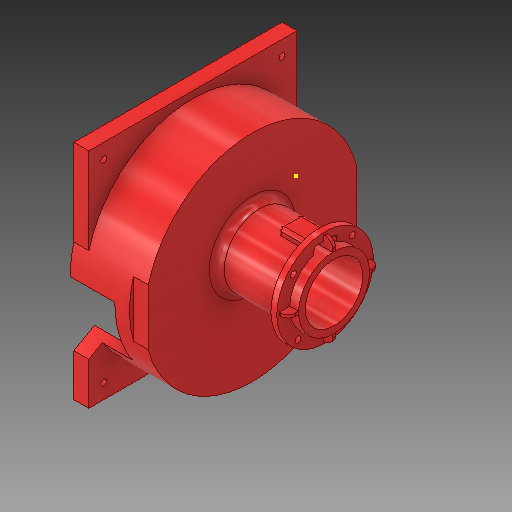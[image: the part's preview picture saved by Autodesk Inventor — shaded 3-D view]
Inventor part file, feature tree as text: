
AUTODESK INVENTOR PART (.ipt)
format: ipt  version: 2019 (Build 230136000, 136)  size: 1,012,736 bytes
history: native  units: mm
features: sketch x42, extrude x40, projected_geometry x19, other x6, fillet x6, reference x2
ambient origin geometry x8: Origin, YZ Plane, XZ Plane, XY Plane, X Axis, Y Axis, Z Axis, Center Point
bodies: Body1 (feature_tree)
feature tree (115):
  other  "Твердое тело1"
  other  "0ae4c1a17e304db4a8c8e39318f74883.stl"
  extrude  "Выдавливание1"  Depth=3.0mm TaperAngle=0.0deg
  extrude  "Выдавливание2"  Depth=43.0mm
  extrude  "Выдавливание3"  Depth=25.0mm TaperAngle=0.0deg
  extrude  "Выдавливание4"  Depth=20.0mm
  extrude  "Выдавливание5"  Depth=20.0mm
  extrude  "Выдавливание6"  Depth=50.0mm TaperAngle=0.0deg
  extrude  "Выдавливание7"  Depth=34.0mm
  extrude  "Выдавливание8"  Depth=2.0mm
  extrude  "Выдавливание9"  Depth=2.0mm
  extrude  "Выдавливание10"  Depth=1.0mm TaperAngle=0.0deg
  sketch  "Эскиз15"
  sketch  "Эскиз16"
  extrude  "Выдавливание11"  Depth=25.0mm TaperAngle=0.0deg
  extrude  "Выдавливание12"  Depth=4.0mm
  extrude  "Выдавливание13"  Depth=4.0mm
  extrude  "Выдавливание14"  Depth=4.0mm
  extrude  "Выдавливание15"  Depth=4.0mm
  extrude  "Выдавливание16"  Depth=4.5mm
  fillet  "Сопряжение1"  Radius=4.5mm
  fillet  "Сопряжение2"  Radius=4.5mm
  extrude  "Выдавливание17"  Depth=4.5mm
  extrude  "Выдавливание18"  Depth=25.0mm TaperAngle=0.0deg
  extrude  "Выдавливание19"  Depth=7.2mm
  extrude  "Выдавливание20"  Depth=7.2mm
  extrude  "Выдавливание21"  Depth=7.2mm
  extrude  "Выдавливание22"  Depth=7.2mm
  fillet  "Сопряжение3"  Radius=2.0mm
  extrude  "Выдавливание23"  Depth=15.0mm TaperAngle=0.0deg
  extrude  "Выдавливание24"  Depth=15.0mm
  extrude  "Выдавливание25"  Depth=3.0mm
  extrude  "Выдавливание26"  Depth=13.663525mm
  extrude  "Выдавливание27"  Depth=30.32705mm
  extrude  "Выдавливание28"  Depth=8.5mm TaperAngle=0.0deg
  fillet  "Сопряжение4"  Radius=8.5mm
  extrude  "Выдавливание29"  Depth=38.8mm
  extrude  "Выдавливание30"  Depth=22.0mm TaperAngle=0.0deg
  extrude  "Выдавливание31"  Depth=25.0mm TaperAngle=0.0deg
  extrude  "Выдавливание32"  Depth=10.0mm TaperAngle=0.0deg
  fillet  "Сопряжение5"  Radius=3.5mm
  sketch  "Эскиз38"
  extrude  "Выдавливание33"  Depth=3.5mm TaperAngle=0.0deg
  extrude  "Выдавливание34"  Depth=1.0mm TaperAngle=0.0deg
  extrude  "Выдавливание35"  Depth=2.0mm
  fillet  "Сопряжение6"  Radius=2.0mm
  extrude  "Выдавливание37"  Depth=10.0mm TaperAngle=0.0deg
  extrude  "Выдавливание38"  Depth=3.0mm TaperAngle=0.0deg
  extrude  "Выдавливание39"  Depth=3.0mm TaperAngle=0.0deg
  extrude  "Выдавливание40"  Depth=28.0mm
  extrude  "Выдавливание41"  TaperAngle=135.0deg  [1 undecoded]
  sketch  "Эскиз2"
  sketch  "Эскиз3"
  sketch  "Эскиз5"
  sketch  "Эскиз6"
  projected_geometry  "Спроецированная петля1"
  sketch  "Эскиз8"
  sketch  "Эскиз9"
  projected_geometry  "Спроецированная петля3"
  sketch  "Эскиз11"
  sketch  "Эскиз12"
  projected_geometry  "Спроецированная петля4"
  sketch  "Эскиз13"
  sketch  "Эскиз14"
  sketch  "Эскиз17"
  sketch  "Эскиз18"
  projected_geometry  "Спроецированная петля5"
  sketch  "Эскиз19"
  projected_geometry  "Спроецированная петля6"
  projected_geometry  "Спроецированная петля7"
  sketch  "Эскиз20"
  projected_geometry  "Спроецированная петля8"
  sketch  "Эскиз21"
  projected_geometry  "Спроецированная петля9"
  sketch  "Эскиз22"
  projected_geometry  "Спроецированная петля10"
  sketch  "Эскиз23"
  sketch  "Эскиз24"
  sketch  "Эскиз25"
  sketch  "Эскиз26"
  sketch  "Эскиз27"
  sketch  "Эскиз28"
  sketch  "Эскиз29"
  sketch  "Эскиз30"
  sketch  "Эскиз31"
  projected_geometry  "Спроецированная петля11"
  sketch  "Эскиз32"
  projected_geometry  "Спроецированная петля12"
  sketch  "Эскиз33"
  sketch  "Эскиз34"
  sketch  "Эскиз35"
  projected_geometry  "Спроецированная петля13"
  sketch  "Эскиз36"
  sketch  "Эскиз37"
  sketch  "Эскиз39"
  projected_geometry  "Спроецированная петля14"
  sketch  "Эскиз40"
  projected_geometry  "Спроецированная петля15"
  sketch  "Эскиз41"
  sketch  "Эскиз43"
  projected_geometry  "Спроецированная петля17"
  sketch  "Эскиз44"
  reference  "Ссылка1"
  sketch  "Эскиз45"
  projected_geometry  "Спроецированная петля18"
  projected_geometry  "Спроецированная петля19"
  sketch  "Эскиз46"
  projected_geometry  "Спроецированная петля20"
  projected_geometry  "Спроецированная петля21"
  sketch  "Эскиз47"
  reference  "Ссылка2"
  other  "ЭлементСетки1"
  parser-record x1  (decoder bookkeeping rows leaked as tree rows — omitted from the tree; the rows remain in map.json)
  other  "kowsh.iam"
  other  "Барабан:1"
note: 1 required parameter value undecoded (feature->parameter linkage not recoverable at this tier; creation-order binding heuristic only, values carry confidence <= 0.55)
note: 1 file-system path scrubbed to <path> (originals preserved in map.json)
